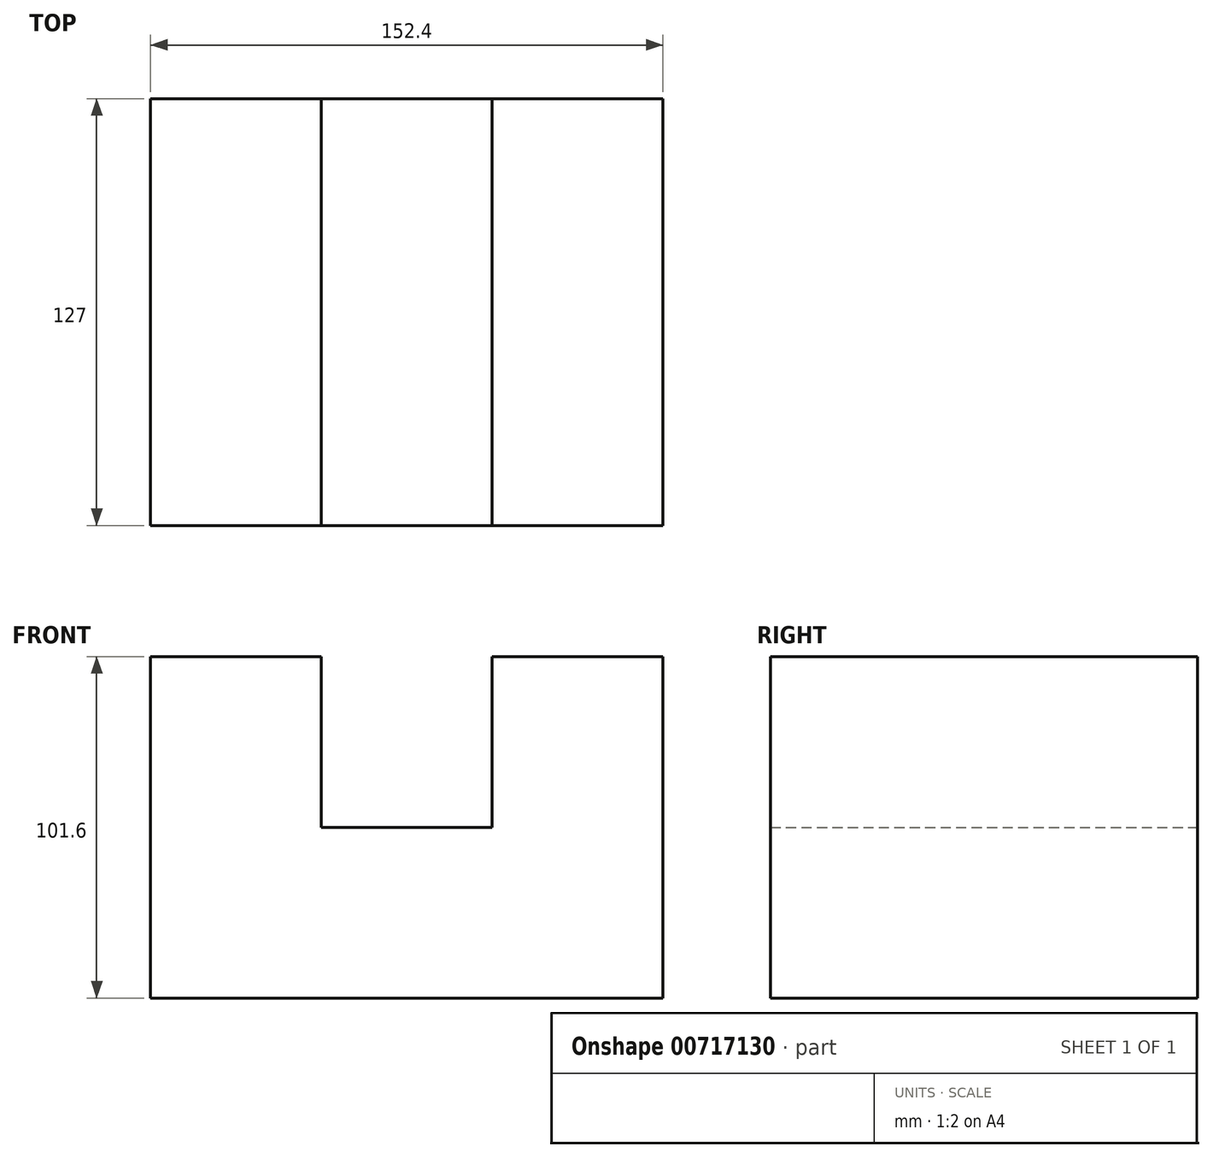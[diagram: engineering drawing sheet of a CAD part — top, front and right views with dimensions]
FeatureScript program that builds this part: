
annotation { "Feature Type Name" : "Feature", "Feature Type Description" : "" }
export const myFeature = defineFeature(function(context is Context, id is Id, definition is map)
    precondition{}
    {
        {
            var Q0;
            Q0=qCreatedBy(makeId("Front.planeOp"),FACE);
            var sketch = newSketch(context, id + "F0", { "sketchPlane" : qUnion([Q0])});
            skLineSegment(sketch, "E0", {"start": v(-124.83, -50.8) * mm, "end": v(27.57, -50.8) * mm});
            skLineSegment(sketch, "E1", {"start": v(27.57, -50.8) * mm, "end": v(27.57, 50.8) * mm});
            skLineSegment(sketch, "E2", {"start": v(27.57, 50.8) * mm, "end": v(-23.23, 50.8) * mm});
            skLineSegment(sketch, "E3", {"start": v(-23.23, 50.8) * mm, "end": v(-23.23, 0) * mm});
            skLineSegment(sketch, "E4", {"start": v(-23.23, 0) * mm, "end": v(-74.03, 0) * mm});
            skLineSegment(sketch, "E5", {"start": v(-74.03, 0) * mm, "end": v(-74.03, 50.8) * mm});
            skLineSegment(sketch, "E6", {"start": v(-74.03, 50.8) * mm, "end": v(-124.83, 50.8) * mm});
            skLineSegment(sketch, "E7", {"start": v(-124.83, 50.8) * mm, "end": v(-124.83, -50.8) * mm});
            skSolve(sketch);
        }
        {
            var Q0;
            Q0=makeQuery(id+"F0.imprint","IMPRINT",FACE,{"disambiguationData":[TD([[makeQuery(id+"F0.imprint","IMPRINT",EDGE,{"derivedFrom":sQuery(id+"F0.wireOp",EDGE,"E0")}),1.0]])]});
            extrude(context, id + "F1", {"entities" : qUnion([Q0]), "depth" : 127 * mm, "offsetDistance" : 25.4 * mm});
        }
    });
